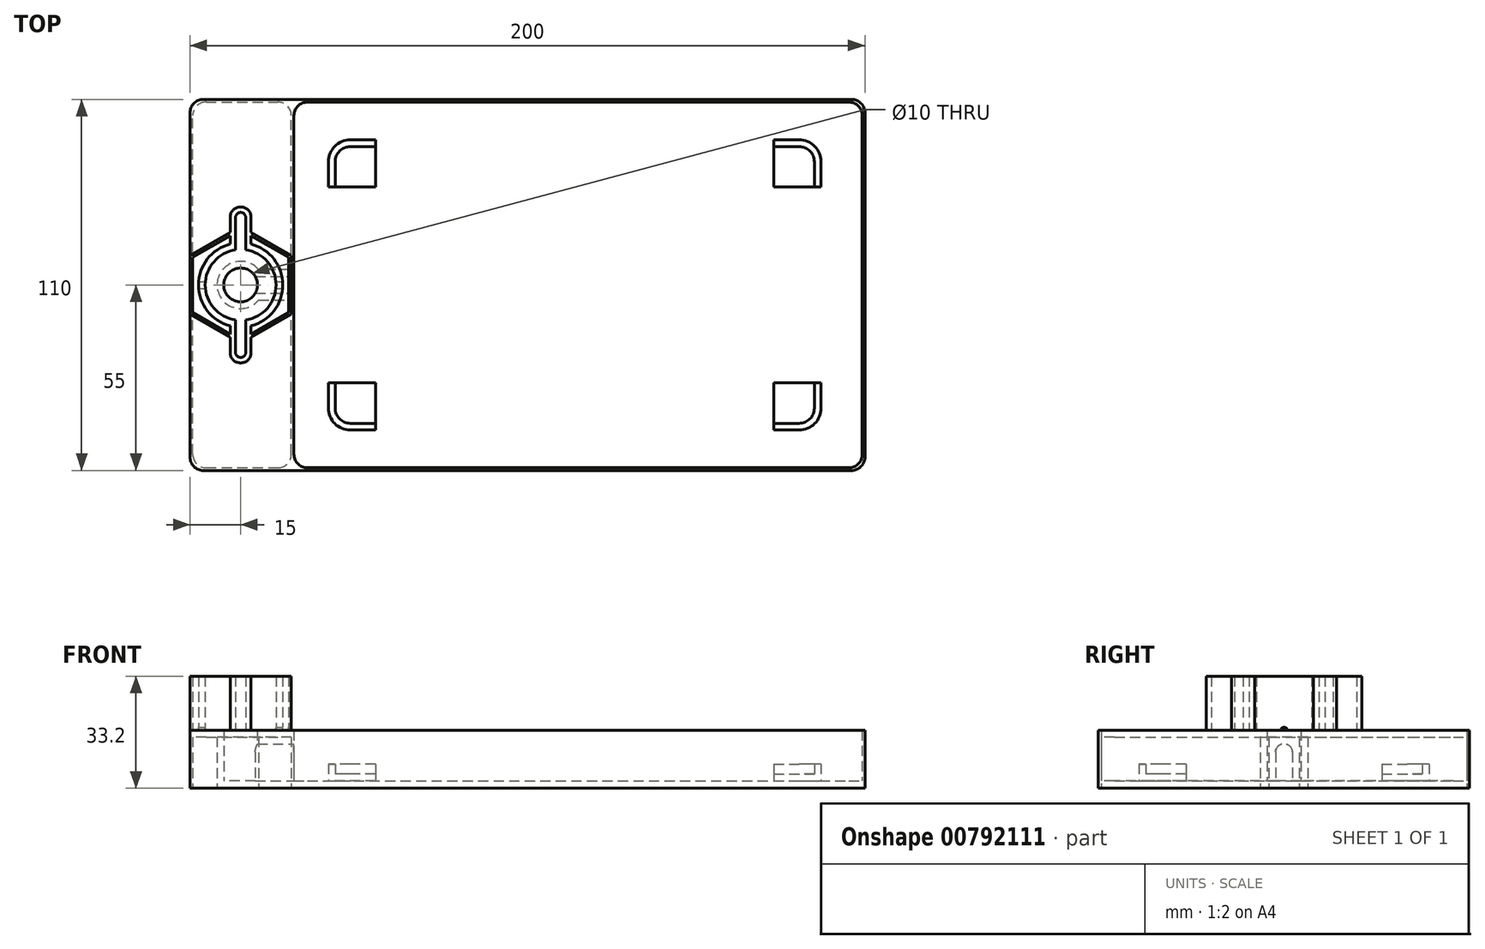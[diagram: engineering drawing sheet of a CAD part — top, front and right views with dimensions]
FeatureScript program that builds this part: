
annotation { "Feature Type Name" : "Feature", "Feature Type Description" : "" }
export const myFeature = defineFeature(function(context is Context, id is Id, definition is map)
    precondition{}
    {
        {
            var Q0;
            Q0=qCreatedBy(makeId("Top.planeOp"),FACE);
            var sketch = newSketch(context, id + "F0", { "sketchPlane" : qUnion([Q0])});
            skLineSegment(sketch, "E0.bottom", {"start": v(-4, 0) * mm, "end": v(-196, 0) * mm});
            skLineSegment(sketch, "E0.top", {"start": v(-4, 110) * mm, "end": v(-196, 110) * mm});
            skLineSegment(sketch, "E0.left", {"start": v(0, 4) * mm, "end": v(0, 106) * mm});
            skLineSegment(sketch, "E0.right", {"start": v(-200, 4) * mm, "end": v(-200, 106) * mm});
            skPoint(sketch, "E1.visualSharp", {"position": v(0, 110) * mm});
            skArc(sketch, "E1.filletArc", {"start": v(0, 106) * mm, "mid": v(-1.17, 108.83) * mm, "end": v(-4, 110) * mm});
            skPoint(sketch, "E2.visualSharp", {"position": v(0, 0) * mm});
            skArc(sketch, "E2.filletArc", {"start": v(-4, 0) * mm, "mid": v(-1.17, 1.17) * mm, "end": v(0, 4) * mm});
            skPoint(sketch, "E3.visualSharp", {"position": v(-200, 0) * mm});
            skArc(sketch, "E3.filletArc", {"start": v(-200, 4) * mm, "mid": v(-198.83, 1.17) * mm, "end": v(-196, 0) * mm});
            skPoint(sketch, "E4.visualSharp", {"position": v(-200, 110) * mm});
            skArc(sketch, "E4.filletArc", {"start": v(-196, 110) * mm, "mid": v(-198.83, 108.83) * mm, "end": v(-200, 106) * mm});
            skLineSegment(sketch, "E5", {"start": v(-0.8, 105.2) * mm, "end": v(-0.8, 4.8) * mm});
            skLineSegment(sketch, "E6", {"start": v(-4.8, 0.8) * mm, "end": v(-165.2, 0.8) * mm});
            skLineSegment(sketch, "E7", {"start": v(-169.2, 4.8) * mm, "end": v(-169.2, 105.2) * mm});
            skLineSegment(sketch, "E8", {"start": v(-165.2, 109.2) * mm, "end": v(-4.8, 109.2) * mm});
            skPoint(sketch, "E9.visualSharp", {"position": v(-169.2, 109.2) * mm});
            skArc(sketch, "E9.filletArc", {"start": v(-165.2, 109.2) * mm, "mid": v(-168.03, 108.03) * mm, "end": v(-169.2, 105.2) * mm});
            skPoint(sketch, "E10.visualSharp", {"position": v(-169.2, 0.8) * mm});
            skArc(sketch, "E10.filletArc", {"start": v(-169.2, 4.8) * mm, "mid": v(-168.03, 1.97) * mm, "end": v(-165.2, 0.8) * mm});
            skPoint(sketch, "E11.visualSharp", {"position": v(-0.8, 0.8) * mm});
            skArc(sketch, "E11.filletArc", {"start": v(-4.8, 0.8) * mm, "mid": v(-1.97, 1.97) * mm, "end": v(-0.8, 4.8) * mm});
            skPoint(sketch, "E12.visualSharp", {"position": v(-0.8, 109.2) * mm});
            skArc(sketch, "E12.filletArc", {"start": v(-0.8, 105.2) * mm, "mid": v(-1.97, 108.03) * mm, "end": v(-4.8, 109.2) * mm});
            skCircle(sketch, "E13", {"center": v(-185, 55) * mm, "radius": 5 * mm});
            skPoint(sketch, "E13.centerSnap0", {"position": v(-200, 55) * mm});
            skCircle(sketch, "E14", {"center": v(-185, 55) * mm, "radius": 7 * mm});
            skLineSegment(sketch, "E15.bottom", {"start": v(-195.2, 0.8) * mm, "end": v(-174, 0.8) * mm});
            skLineSegment(sketch, "E15.top", {"start": v(-195.2, 109.2) * mm, "end": v(-174, 109.2) * mm});
            skLineSegment(sketch, "E15.left", {"start": v(-199.2, 4.8) * mm, "end": v(-199.2, 105.2) * mm});
            skLineSegment(sketch, "E15.right", {"start": v(-170, 4.8) * mm, "end": v(-170, 105.2) * mm});
            skPoint(sketch, "E16.visualSharp", {"position": v(-199.2, 109.2) * mm});
            skArc(sketch, "E16.filletArc", {"start": v(-195.2, 109.2) * mm, "mid": v(-198.03, 108.03) * mm, "end": v(-199.2, 105.2) * mm});
            skPoint(sketch, "E17.visualSharp", {"position": v(-170, 109.2) * mm});
            skArc(sketch, "E17.filletArc", {"start": v(-170, 105.2) * mm, "mid": v(-171.17, 108.03) * mm, "end": v(-174, 109.2) * mm});
            skPoint(sketch, "E18.visualSharp", {"position": v(-199.2, 0.8) * mm});
            skArc(sketch, "E18.filletArc", {"start": v(-199.2, 4.8) * mm, "mid": v(-198.03, 1.97) * mm, "end": v(-195.2, 0.8) * mm});
            skPoint(sketch, "E19.visualSharp", {"position": v(-170, 0.8) * mm});
            skArc(sketch, "E19.filletArc", {"start": v(-174, 0.8) * mm, "mid": v(-171.17, 1.97) * mm, "end": v(-170, 4.8) * mm});
            skLineSegment(sketch, "E20", {"start": v(-179.64, 50.5) * mm, "end": v(-170, 50.5) * mm});
            skLineSegment(sketch, "E21", {"start": v(-170, 59.5) * mm, "end": v(-179.64, 59.5) * mm});
            skSolve(sketch);
        }
        {
            var Q0;
            Q0=makeQuery(id+"F0.imprint","IMPRINT",FACE,{"disambiguationData":[TD([[makeQuery(id+"F0.imprint","IMPRINT",EDGE,{"derivedFrom":sQuery(id+"F0.wireOp",EDGE,"E5")}),-1.0]])]});
            var Q1;
            Q1=makeQuery(id+"F0.imprint","IMPRINT",FACE,{"disambiguationData":[TD([[makeQuery(id+"F0.imprint","IMPRINT",EDGE,{"derivedFrom":sQuery(id+"F0.wireOp",EDGE,"E0.bottom")}),-1.0]])]});
            var Q2;
            Q2=makeQuery(id+"F0.imprint","IMPRINT",FACE,{"disambiguationData":[TD([[makeQuery(id+"F0.imprint","IMPRINT",EDGE,{"derivedFrom":sQuery(id+"F0.wireOp",EDGE,"E13")}),1.0]])]});
            var Q3;
            Q3=makeQuery(id+"F0.imprint","IMPRINT",FACE,{"disambiguationData":[TD([[makeQuery(id+"F0.imprint","IMPRINT",EDGE,{"derivedFrom":sQuery(id+"F0.wireOp",EDGE,"E14")}),-1.0]])]});
            var Q4;
            Q4=makeQuery(id+"F0.imprint","IMPRINT",FACE,{"disambiguationData":[TD([[makeQuery(id+"F0.imprint","IMPRINT",EDGE,{"derivedFrom":sQuery(id+"F0.wireOp",EDGE,"E13")}),-1.0]])]});
            var Q5;
            Q5=makeQuery(id+"F0.imprint","IMPRINT",FACE,{"disambiguationData":[TD([[makeQuery(id+"F0.imprint","IMPRINT",EDGE,{"derivedFrom":sQuery(id+"F0.wireOp",EDGE,"E15.bottom")}),1.0]])]});
            extrude(context, id + "F1", {"entities" : qUnion([Q0, Q1, Q2, Q3, Q4, Q5]), "depth" : 2.2 * mm, "offsetDistance" : 25 * mm});
        }
        {
            var Q0;
            Q0=makeQuery(id+"F0.imprint","IMPRINT",FACE,{"disambiguationData":[TD([[makeQuery(id+"F0.imprint","IMPRINT",EDGE,{"derivedFrom":sQuery(id+"F0.wireOp",EDGE,"E0.bottom")}),-1.0]])]});
            var Q1;
            Q1=makeQuery(id+"F0.imprint","IMPRINT",FACE,{"disambiguationData":[TD([[makeQuery(id+"F0.imprint","IMPRINT",EDGE,{"derivedFrom":sQuery(id+"F0.wireOp",EDGE,"E13")}),-1.0]])]});
            var Q2;
            Q2=makeQuery(id+"F0.imprint","IMPRINT",FACE,{"disambiguationData":[TD([[makeQuery(id+"F0.imprint","IMPRINT",EDGE,{"derivedFrom":sQuery(id+"F0.wireOp",EDGE,"E15.bottom")}),1.0]])]});
            var Q3;
            {var subQ0=sQuery(id+"F0.wireOp",EDGE,"E20");Q3=makeQuery(id+"F0.imprint","IMPRINT",FACE,{"disambiguationData":[TD([[makeQuery(id+"F0.imprint","IMPRINT",EDGE,{"derivedFrom":subQ0}),1.0]])]});}
            extrude(context, id + "F2", {"entities" : qUnion([Q0, Q1, Q2, Q3]), "operationType" : NewBodyOperationType.ADD, "depth" : 17.2 * mm, "offsetDistance" : 25 * mm});
        }
        {
            var Q0;
            Q0=makeQuery(id+"F2.opExtrude","SWEPT_FACE",FACE,{"disambiguationData":[OSD([sQuery(id+"F0.wireOp",EDGE,"E7")])]});
            var sketch = newSketch(context, id + "F3", { "sketchPlane" : qUnion([Q0])});
            skLineSegment(sketch, "E22.bottom", {"start": v(55, 13.2) * mm, "end": v(55, 13.2) * mm});
            skLineSegment(sketch, "E22.top", {"start": v(57.5, 2.2) * mm, "end": v(52.5, 2.2) * mm});
            skLineSegment(sketch, "E22.left", {"start": v(57.5, 10.7) * mm, "end": v(57.5, 2.2) * mm});
            skLineSegment(sketch, "E22.right", {"start": v(52.5, 10.7) * mm, "end": v(52.5, 2.2) * mm});
            skPoint(sketch, "E23.visualSharp", {"position": v(52.5, 13.2) * mm});
            skArc(sketch, "E23.filletArc", {"start": v(55, 13.2) * mm, "mid": v(53.23, 12.47) * mm, "end": v(52.5, 10.7) * mm});
            skPoint(sketch, "E24.visualSharp", {"position": v(57.5, 13.2) * mm});
            skArc(sketch, "E24.filletArc", {"start": v(57.5, 10.7) * mm, "mid": v(56.77, 12.47) * mm, "end": v(55, 13.2) * mm});
            skSolve(sketch);
        }
        {
            var Q0;
            Q0=makeQuery(id+"F3.imprint","IMPRINT",FACE,{"disambiguationData":[TD([[makeQuery(id+"F3.imprint","IMPRINT",EDGE,{"derivedFrom":sQuery(id+"F3.wireOp",EDGE,"E22.top")}),-1.0]])]});
            extrude(context, id + "F4", {"entities" : qUnion([Q0]), "operationType" : NewBodyOperationType.REMOVE, "oppositeDirection" : true, "depth" : 20 * mm, "offsetDistance" : 25 * mm});
        }
        {
            var Q0;
            Q0=makeQuery(id+"F0.imprint","IMPRINT",FACE,{"disambiguationData":[TD([[makeQuery(id+"F0.imprint","IMPRINT",EDGE,{"derivedFrom":sQuery(id+"F0.wireOp",EDGE,"E15.bottom")}),1.0]])]});
            extrude(context, id + "F5", {"entities" : qUnion([Q0]), "operationType" : NewBodyOperationType.REMOVE, "depth" : 15.2 * mm, "offsetDistance" : 25 * mm});
        }
        {
            var Q0;
            Q0=makeQuery(id+"F2.opExtrude","CAP_FACE",FACE,{"disambiguationData":[OSD([sQuery(id+"F0.wireOp",EDGE,"E0.bottom"),sQuery(id+"F0.wireOp",EDGE,"E0.top"),sQuery(id+"F0.wireOp",EDGE,"E0.left"),sQuery(id+"F0.wireOp",EDGE,"E0.right"),sQuery(id+"F0.wireOp",EDGE,"E1.filletArc"),sQuery(id+"F0.wireOp",EDGE,"E2.filletArc"),sQuery(id+"F0.wireOp",EDGE,"E3.filletArc"),sQuery(id+"F0.wireOp",EDGE,"E4.filletArc"),sQuery(id+"F0.wireOp",EDGE,"E5"),sQuery(id+"F0.wireOp",EDGE,"E6"),sQuery(id+"F0.wireOp",EDGE,"E7"),sQuery(id+"F0.wireOp",EDGE,"E8"),sQuery(id+"F0.wireOp",EDGE,"E9.filletArc"),sQuery(id+"F0.wireOp",EDGE,"E10.filletArc"),sQuery(id+"F0.wireOp",EDGE,"E11.filletArc"),sQuery(id+"F0.wireOp",EDGE,"E12.filletArc"),sQuery(id+"F0.wireOp",EDGE,"E13")])],"isStart":false});
            var sketch = newSketch(context, id + "F6", { "sketchPlane" : qUnion([Q0])});
            skCircle(sketch, "E25", {"center": v(-185, 55) * mm, "radius": 10.5 * mm});
            skCircle(sketch, "E26", {"center": v(-185, 55) * mm, "radius": 12.5 * mm});
            skLineSegment(sketch, "E27", {"start": v(-186.5, 67.4) * mm, "end": v(-186.5, 75) * mm});
            skLineSegment(sketch, "E28", {"start": v(-185, 76.5) * mm, "end": v(-185, 76.5) * mm});
            skLineSegment(sketch, "E29", {"start": v(-183.5, 75) * mm, "end": v(-183.5, 67.4) * mm});
            skLineSegment(sketch, "E30", {"start": v(-188.1, 67.1) * mm, "end": v(-188.1, 75.1) * mm});
            skLineSegment(sketch, "E31", {"start": v(-185.1, 78.1) * mm, "end": v(-184.9, 78.1) * mm});
            skLineSegment(sketch, "E32", {"start": v(-181.9, 75.1) * mm, "end": v(-181.9, 67.1) * mm});
            skLineSegment(sketch, "E33", {"start": v(-174.5, 55) * mm, "end": v(-195.5, 55) * mm, "construction": true});
            skLineSegment(sketch, "E34.MirrorCS", {"start": v(-185.1, 31.9) * mm, "end": v(-184.9, 31.9) * mm});
            skLineSegment(sketch, "E35.MirrorCS", {"start": v(-188.1, 42.9) * mm, "end": v(-188.1, 34.9) * mm});
            skLineSegment(sketch, "E36.MirrorCS", {"start": v(-186.5, 42.6) * mm, "end": v(-186.5, 35) * mm});
            skLineSegment(sketch, "E37.MirrorCS", {"start": v(-183.5, 35) * mm, "end": v(-183.5, 42.6) * mm});
            skLineSegment(sketch, "E38.MirrorCS", {"start": v(-181.9, 34.9) * mm, "end": v(-181.9, 42.9) * mm});
            skLineSegment(sketch, "E39.MirrorCS", {"start": v(-185, 33.5) * mm, "end": v(-185, 33.5) * mm});
            skLineSegment(sketch, "E40", {"start": v(-186.5, 67.4) * mm, "end": v(-186.5, 65.4) * mm});
            skLineSegment(sketch, "E41", {"start": v(-183.5, 67.4) * mm, "end": v(-183.5, 65.4) * mm});
            skLineSegment(sketch, "E42", {"start": v(-186.5, 42.6) * mm, "end": v(-186.5, 44.6) * mm});
            skLineSegment(sketch, "E43", {"start": v(-183.5, 42.6) * mm, "end": v(-183.5, 44.6) * mm});
            skPoint(sketch, "E44.visualSharp", {"position": v(-183.5, 76.5) * mm});
            skArc(sketch, "E44.filletArc", {"start": v(-183.5, 75) * mm, "mid": v(-183.94, 76.06) * mm, "end": v(-185, 76.5) * mm});
            skPoint(sketch, "E45.visualSharp", {"position": v(-186.5, 76.5) * mm});
            skArc(sketch, "E45.filletArc", {"start": v(-185, 76.5) * mm, "mid": v(-186.06, 76.06) * mm, "end": v(-186.5, 75) * mm});
            skPoint(sketch, "E46.visualSharp", {"position": v(-188.1, 78.1) * mm});
            skArc(sketch, "E46.filletArc", {"start": v(-185.1, 78.1) * mm, "mid": v(-187.22, 77.22) * mm, "end": v(-188.1, 75.1) * mm});
            skPoint(sketch, "E47.visualSharp", {"position": v(-181.9, 78.1) * mm});
            skArc(sketch, "E47.filletArc", {"start": v(-181.9, 75.1) * mm, "mid": v(-182.78, 77.22) * mm, "end": v(-184.9, 78.1) * mm});
            skPoint(sketch, "E48.visualSharp", {"position": v(-188.1, 31.9) * mm});
            skArc(sketch, "E48.filletArc", {"start": v(-188.1, 34.9) * mm, "mid": v(-187.22, 32.78) * mm, "end": v(-185.1, 31.9) * mm});
            skPoint(sketch, "E49.visualSharp", {"position": v(-181.9, 31.9) * mm});
            skArc(sketch, "E49.filletArc", {"start": v(-184.9, 31.9) * mm, "mid": v(-182.78, 32.78) * mm, "end": v(-181.9, 34.9) * mm});
            skPoint(sketch, "E50.visualSharp", {"position": v(-186.5, 33.5) * mm});
            skArc(sketch, "E50.filletArc", {"start": v(-186.5, 35) * mm, "mid": v(-186.06, 33.94) * mm, "end": v(-185, 33.5) * mm});
            skPoint(sketch, "E51.visualSharp", {"position": v(-183.5, 33.5) * mm});
            skArc(sketch, "E51.filletArc", {"start": v(-185, 33.5) * mm, "mid": v(-183.94, 33.94) * mm, "end": v(-183.5, 35) * mm});
            skSolve(sketch);
        }
        {
            var Q0;
            {var subQ4=sQuery(id+"F6.wireOp",EDGE,"E40");Q0=makeQuery(id+"F6.imprint","IMPRINT",FACE,{"disambiguationData":[TD([[makeQuery(id+"F6.imprint","IMPRINT",EDGE,{"derivedFrom":subQ4}),-1.0]])]});}
            var Q1;
            {var subQ0=sQuery(id+"F6.wireOp",EDGE,"E27");Q1=makeQuery(id+"F6.imprint","IMPRINT",FACE,{"disambiguationData":[TD([[makeQuery(id+"F6.imprint","IMPRINT",EDGE,{"derivedFrom":subQ0}),1.0]])]});}
            var Q2;
            {var subQ4=sQuery(id+"F6.wireOp",EDGE,"E41");Q2=makeQuery(id+"F6.imprint","IMPRINT",FACE,{"disambiguationData":[TD([[makeQuery(id+"F6.imprint","IMPRINT",EDGE,{"derivedFrom":subQ4}),1.0]])]});}
            var Q3;
            Q3=makeQuery(id+"F6.imprint","IMPRINT",FACE,{"disambiguationData":[TD([[makeQuery(id+"F6.imprint","IMPRINT",EDGE,{"derivedFrom":sQuery(id+"F6.wireOp",EDGE,"E34.MirrorCS")}),1.0]])]});
            extrude(context, id + "F7", {"entities" : qUnion([Q0, Q1, Q2, Q3]), "operationType" : NewBodyOperationType.ADD, "depth" : 16 * mm, "offsetDistance" : 25 * mm});
        }
        {
            var Q0;
            {var subQ0=makeQuery(id+"F1.opExtrude","CAP_FACE",FACE,{"disambiguationData":[OSD([sQuery(id+"F0.wireOp",EDGE,"E0.bottom"),sQuery(id+"F0.wireOp",EDGE,"E0.top"),sQuery(id+"F0.wireOp",EDGE,"E0.left"),sQuery(id+"F0.wireOp",EDGE,"E0.right"),sQuery(id+"F0.wireOp",EDGE,"E1.filletArc"),sQuery(id+"F0.wireOp",EDGE,"E2.filletArc"),sQuery(id+"F0.wireOp",EDGE,"E3.filletArc"),sQuery(id+"F0.wireOp",EDGE,"E4.filletArc")])],"isStart":false});Q0=makeQuery(id+"F4.boolean.opBoolean","MERGE",FACE,{"derivedFrom":[makeQuery(id+"F2.boolean.opBoolean","SPLIT",FACE,{"disambiguationData":[TD([makeQuery(id+"F2.opExtrude","SWEPT_FACE",FACE,{"disambiguationData":[OSD([sQuery(id+"F0.wireOp",EDGE,"E13")])]})])],"derivedFrom":subQ0}),makeQuery(id+"F2.boolean.opBoolean","SPLIT",FACE,{"disambiguationData":[TD([makeQuery(id+"F2.opExtrude","SWEPT_FACE",FACE,{"disambiguationData":[OSD([sQuery(id+"F0.wireOp",EDGE,"E5")])]})])],"derivedFrom":subQ0})],"fromTools":[makeQuery(id+"F4.opExtrude","SWEPT_FACE",FACE,{"disambiguationData":[OSD([sQuery(id+"F3.wireOp",EDGE,"E22.top")])]})]});}
            var sketch = newSketch(context, id + "F8", { "sketchPlane" : qUnion([Q0])});
            skLineSegment(sketch, "E52.bottom", {"start": v(-145, 84) * mm, "end": v(-157, 84) * mm});
            skLineSegment(sketch, "E52.top", {"start": v(-145, 96) * mm, "end": v(-152.5, 96) * mm});
            skLineSegment(sketch, "E52.left", {"start": v(-145, 84) * mm, "end": v(-145, 96) * mm});
            skLineSegment(sketch, "E52.right", {"start": v(-157, 84) * mm, "end": v(-157, 91.5) * mm});
            skLineSegment(sketch, "E53.bottom", {"start": v(-145, 26) * mm, "end": v(-157, 26) * mm});
            skLineSegment(sketch, "E53.top", {"start": v(-145, 14) * mm, "end": v(-152.5, 14) * mm});
            skLineSegment(sketch, "E53.left", {"start": v(-145, 26) * mm, "end": v(-145, 14) * mm});
            skLineSegment(sketch, "E53.right", {"start": v(-157, 26) * mm, "end": v(-157, 18.5) * mm});
            skLineSegment(sketch, "E54.bottom", {"start": v(-27, 96) * mm, "end": v(-19.5, 96) * mm});
            skLineSegment(sketch, "E54.top", {"start": v(-27, 84) * mm, "end": v(-15, 84) * mm});
            skLineSegment(sketch, "E54.left", {"start": v(-27, 96) * mm, "end": v(-27, 84) * mm});
            skLineSegment(sketch, "E54.right", {"start": v(-15, 91.5) * mm, "end": v(-15, 84) * mm});
            skPoint(sketch, "E55.firstSnap0", {"position": v(-151, 26) * mm});
            skPoint(sketch, "E55.firstSnap1", {"position": v(-27, 90) * mm});
            skLineSegment(sketch, "E55.bottom", {"start": v(-27, 26) * mm, "end": v(-15, 26) * mm});
            skLineSegment(sketch, "E55.top", {"start": v(-27, 14) * mm, "end": v(-19.5, 14) * mm});
            skLineSegment(sketch, "E55.left", {"start": v(-27, 26) * mm, "end": v(-27, 14) * mm});
            skLineSegment(sketch, "E55.right", {"start": v(-15, 26) * mm, "end": v(-15, 18.5) * mm});
            skPoint(sketch, "E56.visualSharp", {"position": v(-157, 96) * mm});
            skArc(sketch, "E56.filletArc", {"start": v(-152.5, 96) * mm, "mid": v(-155.68, 94.68) * mm, "end": v(-157, 91.5) * mm});
            skPoint(sketch, "E57.visualSharp", {"position": v(-157, 14) * mm});
            skArc(sketch, "E57.filletArc", {"start": v(-157, 18.5) * mm, "mid": v(-155.68, 15.32) * mm, "end": v(-152.5, 14) * mm});
            skPoint(sketch, "E58.visualSharp", {"position": v(-15, 14) * mm});
            skArc(sketch, "E58.filletArc", {"start": v(-19.5, 14) * mm, "mid": v(-16.32, 15.32) * mm, "end": v(-15, 18.5) * mm});
            skPoint(sketch, "E59.visualSharp", {"position": v(-15, 96) * mm});
            skArc(sketch, "E59.filletArc", {"start": v(-15, 91.5) * mm, "mid": v(-16.32, 94.68) * mm, "end": v(-19.5, 96) * mm});
            skLineSegment(sketch, "E60.0", {"start": v(-159, 84) * mm, "end": v(-159, 91.5) * mm});
            skArc(sketch, "E60.1", {"start": v(-152.5, 98) * mm, "mid": v(-157.1, 96.1) * mm, "end": v(-159, 91.5) * mm});
            skLineSegment(sketch, "E60.2", {"start": v(-145, 98) * mm, "end": v(-152.5, 98) * mm});
            skLineSegment(sketch, "E61", {"start": v(-145, 98) * mm, "end": v(-145, 96) * mm});
            skLineSegment(sketch, "E62", {"start": v(-159, 84) * mm, "end": v(-157, 84) * mm});
            skLineSegment(sketch, "E63.0", {"start": v(-27, 98) * mm, "end": v(-19.5, 98) * mm});
            skArc(sketch, "E63.1", {"start": v(-13, 91.5) * mm, "mid": v(-14.9, 96.1) * mm, "end": v(-19.5, 98) * mm});
            skLineSegment(sketch, "E63.2", {"start": v(-13, 91.5) * mm, "end": v(-13, 84) * mm});
            skLineSegment(sketch, "E64", {"start": v(-27, 98) * mm, "end": v(-27, 96) * mm});
            skLineSegment(sketch, "E65", {"start": v(-13, 84) * mm, "end": v(-15, 84) * mm});
            skLineSegment(sketch, "E66.0", {"start": v(-27, 12) * mm, "end": v(-19.5, 12) * mm});
            skArc(sketch, "E66.1", {"start": v(-19.5, 12) * mm, "mid": v(-14.9, 13.9) * mm, "end": v(-13, 18.5) * mm});
            skLineSegment(sketch, "E66.2", {"start": v(-13, 26) * mm, "end": v(-13, 18.5) * mm});
            skLineSegment(sketch, "E67", {"start": v(-27, 12) * mm, "end": v(-27, 14) * mm});
            skLineSegment(sketch, "E68", {"start": v(-13, 26) * mm, "end": v(-15, 26) * mm});
            skLineSegment(sketch, "E69.0", {"start": v(-145, 12) * mm, "end": v(-152.5, 12) * mm});
            skArc(sketch, "E69.1", {"start": v(-159, 18.5) * mm, "mid": v(-157.1, 13.9) * mm, "end": v(-152.5, 12) * mm});
            skLineSegment(sketch, "E69.2", {"start": v(-159, 26) * mm, "end": v(-159, 18.5) * mm});
            skLineSegment(sketch, "E70", {"start": v(-159, 26) * mm, "end": v(-157, 26) * mm});
            skLineSegment(sketch, "E71", {"start": v(-145, 12) * mm, "end": v(-145, 14) * mm});
            skSolve(sketch);
        }
        {
            var Q0;
            Q0=makeQuery(id+"F8.imprint","IMPRINT",FACE,{"disambiguationData":[TD([[makeQuery(id+"F8.imprint","IMPRINT",EDGE,{"derivedFrom":sQuery(id+"F8.wireOp",EDGE,"E52.bottom")}),-1.0]])]});
            var Q1;
            Q1=makeQuery(id+"F8.imprint","IMPRINT",FACE,{"disambiguationData":[TD([[makeQuery(id+"F8.imprint","IMPRINT",EDGE,{"derivedFrom":sQuery(id+"F8.wireOp",EDGE,"E54.bottom")}),-1.0]])]});
            var Q2;
            Q2=makeQuery(id+"F8.imprint","IMPRINT",FACE,{"disambiguationData":[TD([[makeQuery(id+"F8.imprint","IMPRINT",EDGE,{"derivedFrom":sQuery(id+"F8.wireOp",EDGE,"E55.bottom")}),-1.0]])]});
            var Q3;
            Q3=makeQuery(id+"F8.imprint","IMPRINT",FACE,{"disambiguationData":[TD([[makeQuery(id+"F8.imprint","IMPRINT",EDGE,{"derivedFrom":sQuery(id+"F8.wireOp",EDGE,"E53.bottom")}),1.0]])]});
            extrude(context, id + "F9", {"entities" : qUnion([Q0, Q1, Q2, Q3]), "operationType" : NewBodyOperationType.ADD, "depth" : 2 * mm, "offsetDistance" : 25 * mm});
        }
        {
            var Q0;
            Q0=makeQuery(id+"F8.imprint","IMPRINT",FACE,{"disambiguationData":[TD([[makeQuery(id+"F8.imprint","IMPRINT",EDGE,{"derivedFrom":sQuery(id+"F8.wireOp",EDGE,"E52.top")}),-1.0]])]});
            var Q1;
            Q1=makeQuery(id+"F8.imprint","IMPRINT",FACE,{"disambiguationData":[TD([[makeQuery(id+"F8.imprint","IMPRINT",EDGE,{"derivedFrom":sQuery(id+"F8.wireOp",EDGE,"E53.top")}),1.0]])]});
            var Q2;
            Q2=makeQuery(id+"F8.imprint","IMPRINT",FACE,{"disambiguationData":[TD([[makeQuery(id+"F8.imprint","IMPRINT",EDGE,{"derivedFrom":sQuery(id+"F8.wireOp",EDGE,"E55.top")}),-1.0]])]});
            var Q3;
            Q3=makeQuery(id+"F8.imprint","IMPRINT",FACE,{"disambiguationData":[TD([[makeQuery(id+"F8.imprint","IMPRINT",EDGE,{"derivedFrom":sQuery(id+"F8.wireOp",EDGE,"E54.bottom")}),1.0]])]});
            extrude(context, id + "F10", {"entities" : qUnion([Q0, Q1, Q2, Q3]), "operationType" : NewBodyOperationType.ADD, "depth" : 5 * mm, "offsetDistance" : 25 * mm});
        }
        {
            var Q0;
            {var subQ0=sQuery(id+"F0.wireOp",EDGE,"E10.filletArc");var subQ1=sQuery(id+"F0.wireOp",EDGE,"E8");var subQ2=sQuery(id+"F0.wireOp",EDGE,"E7");var subQ3=sQuery(id+"F0.wireOp",EDGE,"E6");var subQ4=sQuery(id+"F0.wireOp",EDGE,"E5");var subQ5=sQuery(id+"F0.wireOp",EDGE,"E4.filletArc");var subQ6=sQuery(id+"F0.wireOp",EDGE,"E3.filletArc");var subQ7=sQuery(id+"F0.wireOp",EDGE,"E2.filletArc");var subQ8=sQuery(id+"F0.wireOp",EDGE,"E1.filletArc");var subQ9=sQuery(id+"F0.wireOp",EDGE,"E0.right");var subQ10=sQuery(id+"F0.wireOp",EDGE,"E0.left");var subQ11=sQuery(id+"F0.wireOp",EDGE,"E0.top");var subQ14=sQuery(id+"F0.wireOp",EDGE,"E9.filletArc");var subQ15=sQuery(id+"F0.wireOp",EDGE,"E0.bottom");var subQ17=sQuery(id+"F0.wireOp",EDGE,"E11.filletArc");var subQ18=sQuery(id+"F0.wireOp",EDGE,"E12.filletArc");Q0=makeQuery(id+"F7.boolean.opBoolean","SPLIT",FACE,{"disambiguationData":[TD([makeQuery(id+"F1.opExtrude","SWEPT_FACE",FACE,{"disambiguationData":[OSD([subQ15])]})])],"derivedFrom":makeQuery(id+"F2.opExtrude","CAP_FACE",FACE,{"disambiguationData":[OSD([subQ15,subQ11,subQ10,subQ9,subQ8,subQ7,subQ6,subQ5,subQ4,subQ3,subQ2,subQ1,subQ14,subQ0,subQ17,subQ18,sQuery(id+"F0.wireOp",EDGE,"E13")])],"isStart":false})});}
            var sketch = newSketch(context, id + "F11", { "sketchPlane" : qUnion([Q0])});
            skCircle(sketch, "E72.cCircle", {"center": v(-185, 55) * mm, "radius": 15 * mm, "construction": true});
            skLineSegment(sketch, "E72.0", {"start": v(-200, 46.34) * mm, "end": v(-200, 63.66) * mm});
            skLineSegment(sketch, "E72.1", {"start": v(-200, 63.66) * mm, "end": v(-185, 72.32) * mm});
            skLineSegment(sketch, "E72.2", {"start": v(-185, 72.32) * mm, "end": v(-170, 63.66) * mm});
            skLineSegment(sketch, "E72.3", {"start": v(-170, 63.66) * mm, "end": v(-170, 46.34) * mm});
            skLineSegment(sketch, "E72.4", {"start": v(-170, 46.34) * mm, "end": v(-185, 37.68) * mm});
            skLineSegment(sketch, "E72.5", {"start": v(-185, 37.68) * mm, "end": v(-200, 46.34) * mm});
            skPoint(sketch, "E72.0.midPoint", {"position": v(-200, 55) * mm});
            skCircle(sketch, "E73.cCircle", {"center": v(-185, 55) * mm, "radius": 14.2 * mm, "construction": true});
            skLineSegment(sketch, "E73.0", {"start": v(-199.2, 46.8) * mm, "end": v(-199.2, 63.2) * mm});
            skLineSegment(sketch, "E73.1", {"start": v(-199.2, 63.2) * mm, "end": v(-185, 71.4) * mm});
            skLineSegment(sketch, "E73.2", {"start": v(-185, 71.4) * mm, "end": v(-170.8, 63.2) * mm});
            skLineSegment(sketch, "E73.3", {"start": v(-170.8, 63.2) * mm, "end": v(-170.8, 46.8) * mm});
            skLineSegment(sketch, "E73.4", {"start": v(-170.8, 46.8) * mm, "end": v(-185, 38.6) * mm});
            skLineSegment(sketch, "E73.5", {"start": v(-185, 38.6) * mm, "end": v(-199.2, 46.8) * mm});
            skPoint(sketch, "E73.0.midPoint", {"position": v(-199.2, 55) * mm});
            skSolve(sketch);
        }
        {
            var Q0;
            {var subQ1=sQuery(id+"F11.wireOp",EDGE,"E72.0");Q0=makeQuery(id+"F11.imprint","IMPRINT",FACE,{"disambiguationData":[TD([[makeQuery(id+"F11.imprint","IMPRINT",EDGE,{"derivedFrom":subQ1}),-1.0]])]});}
            var Q1;
            {var subQ1=sQuery(id+"F11.wireOp",EDGE,"E72.3");Q1=makeQuery(id+"F11.imprint","IMPRINT",FACE,{"disambiguationData":[TD([[makeQuery(id+"F11.imprint","IMPRINT",EDGE,{"derivedFrom":subQ1}),-1.0]])]});}
            extrude(context, id + "F12", {"entities" : qUnion([Q0, Q1]), "operationType" : NewBodyOperationType.ADD, "depth" : 16 * mm, "offsetDistance" : 25 * mm});
        }
        {
            var Q0;
            Q0=makeQuery(id+"F12.opExtrude","SWEPT_FACE",FACE,{"disambiguationData":[OSD([sQuery(id+"F11.wireOp",EDGE,"E72.3")])]});
            var sketch = newSketch(context, id + "F13", { "sketchPlane" : qUnion([Q0])});
            skArc(sketch, "E74", {"start": v(56, 17.2) * mm, "mid": v(55, 18.1) * mm, "end": v(54, 17.2) * mm});
            skSolve(sketch);
        }
        {
            var Q0;
            {var subQ0=sQuery(id+"F13.wireOp",EDGE,"E74");Q0=makeQuery(id+"F13.imprint","IMPRINT",FACE,{"disambiguationData":[TD([[makeQuery(id+"F13.imprint","IMPRINT",EDGE,{"derivedFrom":subQ0}),1.0]])]});}
            extrude(context, id + "F14", {"entities" : qUnion([Q0]), "operationType" : NewBodyOperationType.REMOVE, "oppositeDirection" : true, "depth" : 28 * mm, "offsetDistance" : 25 * mm});
        }
    });
